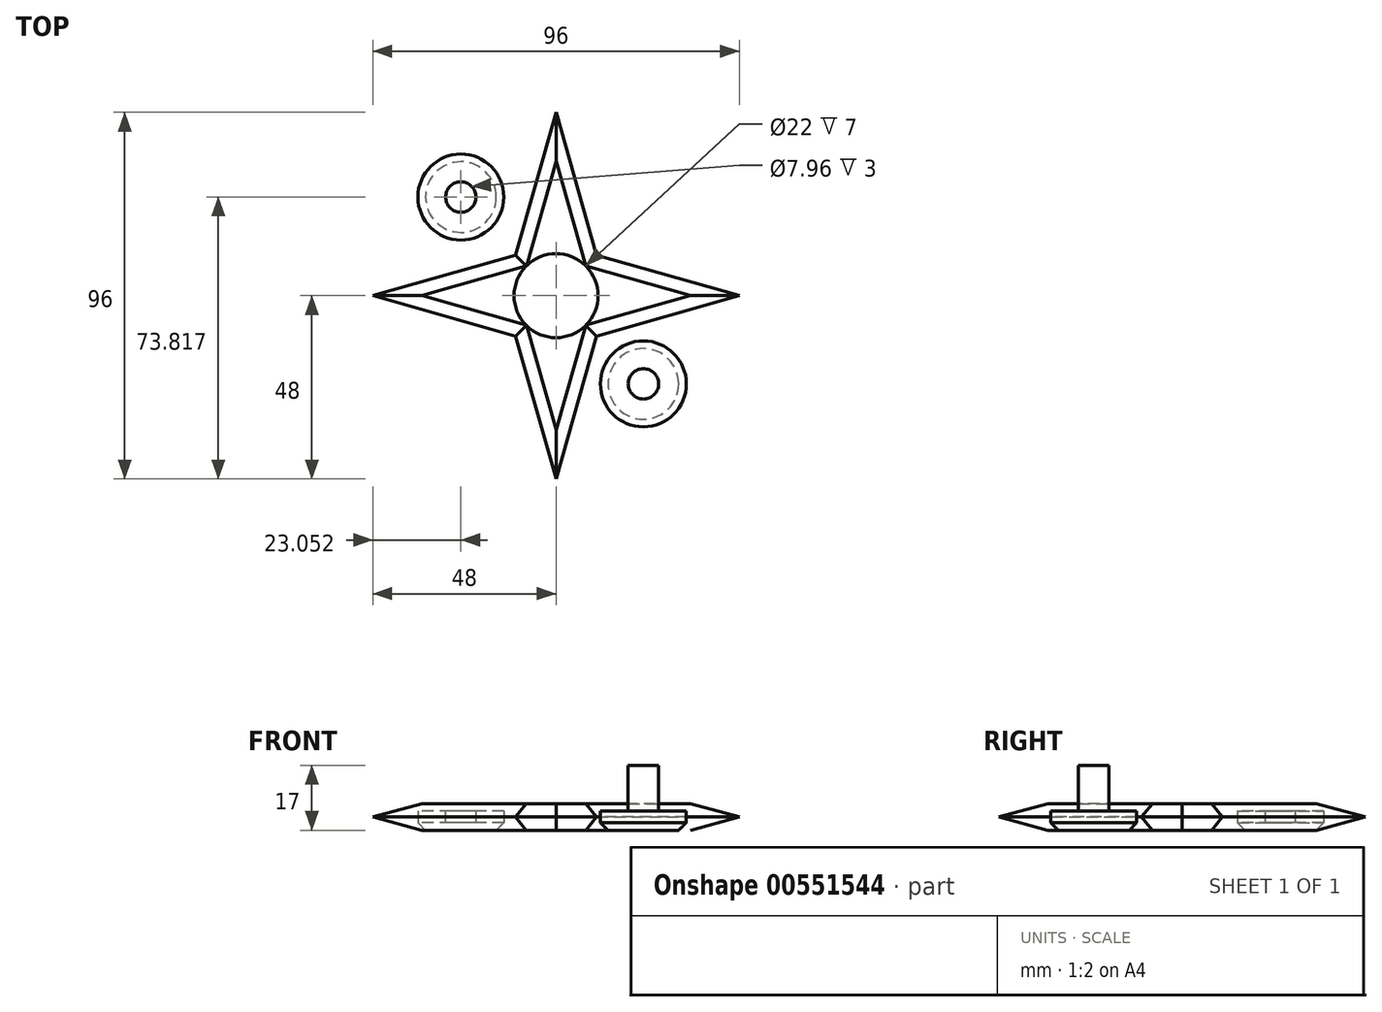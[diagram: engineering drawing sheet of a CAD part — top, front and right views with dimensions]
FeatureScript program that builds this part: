
annotation { "Feature Type Name" : "Feature", "Feature Type Description" : "" }
export const myFeature = defineFeature(function(context is Context, id is Id, definition is map)
    precondition{}
    {
        {
            var Q0;
            Q0=qCreatedBy(makeId("Top.planeOp"),FACE);
            var sketch = newSketch(context, id + "F0", { "sketchPlane" : qUnion([Q0])});
            skCircle(sketch, "E0", {"center": v(0, 0) * mm, "radius": 11 * mm});
            skLineSegment(sketch, "E1", {"start": v(-48, 0) * mm, "end": v(-10.6, 10.6) * mm});
            skLineSegment(sketch, "E2", {"start": v(-10.6, 10.6) * mm, "end": v(0, 48) * mm});
            skLineSegment(sketch, "E3", {"start": v(-48, 0) * mm, "end": v(-10.6, -10.6) * mm});
            skLineSegment(sketch, "E4", {"start": v(-10.6, -10.6) * mm, "end": v(0, -48) * mm});
            skLineSegment(sketch, "E5", {"start": v(0, -48) * mm, "end": v(10.6, -10.6) * mm});
            skLineSegment(sketch, "E6", {"start": v(10.6, -10.6) * mm, "end": v(48, 0) * mm});
            skLineSegment(sketch, "E7", {"start": v(48, 0) * mm, "end": v(10.6, 10.6) * mm});
            skLineSegment(sketch, "E8", {"start": v(10.6, 10.6) * mm, "end": v(0, 48) * mm});
            skSolve(sketch);
        }
        {
            var Q0;
            Q0=makeQuery(id+"F0.imprint","IMPRINT",FACE,{"disambiguationData":[TD([[makeQuery(id+"F0.imprint","IMPRINT",EDGE,{"derivedFrom":sQuery(id+"F0.wireOp",EDGE,"E0")}),-1.0]])]});
            extrude(context, id + "F1", {"entities" : qUnion([Q0]), "depth" : 7 * mm});
        }
        {
            var Q0;
            Q0=makeQuery(id+"F1.opExtrude","CAP_EDGE",EDGE,{"disambiguationData":[OSD([sQuery(id+"F0.wireOp",EDGE,"E2")])],"isStart":false});
            var Q1;
            Q1=makeQuery(id+"F1.opExtrude","CAP_EDGE",EDGE,{"disambiguationData":[OSD([sQuery(id+"F0.wireOp",EDGE,"E8")])],"isStart":false});
            var Q2;
            Q2=makeQuery(id+"F1.opExtrude","CAP_EDGE",EDGE,{"disambiguationData":[OSD([sQuery(id+"F0.wireOp",EDGE,"E7")])],"isStart":false});
            var Q3;
            Q3=makeQuery(id+"F1.opExtrude","CAP_EDGE",EDGE,{"disambiguationData":[OSD([sQuery(id+"F0.wireOp",EDGE,"E6")])],"isStart":false});
            var Q4;
            Q4=makeQuery(id+"F1.opExtrude","CAP_EDGE",EDGE,{"disambiguationData":[OSD([sQuery(id+"F0.wireOp",EDGE,"E5")])],"isStart":false});
            var Q5;
            Q5=makeQuery(id+"F1.opExtrude","CAP_EDGE",EDGE,{"disambiguationData":[OSD([sQuery(id+"F0.wireOp",EDGE,"E4")])],"isStart":false});
            var Q6;
            Q6=makeQuery(id+"F1.opExtrude","CAP_EDGE",EDGE,{"disambiguationData":[OSD([sQuery(id+"F0.wireOp",EDGE,"E3")])],"isStart":false});
            var Q7;
            Q7=makeQuery(id+"F1.opExtrude","CAP_EDGE",EDGE,{"disambiguationData":[OSD([sQuery(id+"F0.wireOp",EDGE,"E1")])],"isStart":false});
            var Q8;
            Q8=makeQuery(id+"F1.opExtrude","CAP_EDGE",EDGE,{"disambiguationData":[OSD([sQuery(id+"F0.wireOp",EDGE,"E3")])],"isStart":true});
            var Q9;
            Q9=makeQuery(id+"F1.opExtrude","CAP_EDGE",EDGE,{"disambiguationData":[OSD([sQuery(id+"F0.wireOp",EDGE,"E1")])],"isStart":true});
            var Q10;
            Q10=makeQuery(id+"F1.opExtrude","CAP_EDGE",EDGE,{"disambiguationData":[OSD([sQuery(id+"F0.wireOp",EDGE,"E2")])],"isStart":true});
            var Q11;
            Q11=makeQuery(id+"F1.opExtrude","CAP_EDGE",EDGE,{"disambiguationData":[OSD([sQuery(id+"F0.wireOp",EDGE,"E4")])],"isStart":true});
            var Q12;
            Q12=makeQuery(id+"F1.opExtrude","CAP_EDGE",EDGE,{"disambiguationData":[OSD([sQuery(id+"F0.wireOp",EDGE,"E5")])],"isStart":true});
            var Q13;
            Q13=makeQuery(id+"F1.opExtrude","CAP_EDGE",EDGE,{"disambiguationData":[OSD([sQuery(id+"F0.wireOp",EDGE,"E6")])],"isStart":true});
            var Q14;
            Q14=makeQuery(id+"F1.opExtrude","CAP_EDGE",EDGE,{"disambiguationData":[OSD([sQuery(id+"F0.wireOp",EDGE,"E7")])],"isStart":true});
            var Q15;
            Q15=makeQuery(id+"F1.opExtrude","CAP_EDGE",EDGE,{"disambiguationData":[OSD([sQuery(id+"F0.wireOp",EDGE,"E8")])],"isStart":true});
            chamfer(context, id + "F2", {"entities" : qUnion([Q0, Q1, Q2, Q3, Q4, Q5, Q6, Q7, Q8, Q9, Q10, Q11, Q12, Q13, Q14, Q15]), "width" : 3.5 * mm, "tangentPropagation" : true});
        }
        {
            var Q0;
            Q0=qCreatedBy(makeId("Top.planeOp"),FACE);
            var sketch = newSketch(context, id + "F3", { "sketchPlane" : qUnion([Q0])});
            skCircle(sketch, "E9", {"center": v(-50.13, 32.9) * mm, "radius": 11.25 * mm});
            skSolve(sketch);
        }
        {
            var Q0;
            Q0=makeQuery(id+"F3.imprint","IMPRINT",FACE,{"disambiguationData":[TD([[makeQuery(id+"F3.imprint","IMPRINT",EDGE,{"derivedFrom":sQuery(id+"F3.wireOp",EDGE,"E9")}),1.0]])]});
            extrude(context, id + "F4", {"entities" : qUnion([Q0]), "depth" : 5 * mm});
        }
        {
            var Q0;
            Q0=makeQuery(id+"F4.opExtrude","CAP_FACE",FACE,{"disambiguationData":[OSD([sQuery(id+"F3.wireOp",EDGE,"E9")])],"isStart":false});
            var sketch = newSketch(context, id + "F5", { "sketchPlane" : qUnion([Q0])});
            skCircle(sketch, "E10", {"center": v(-50.13, 32.9) * mm, "radius": 3.98 * mm});
            skSolve(sketch);
        }
        {
            var Q0;
            Q0=makeQuery(id+"F5.imprint","IMPRINT",FACE,{"disambiguationData":[TD([[makeQuery(id+"F5.imprint","IMPRINT",EDGE,{"derivedFrom":sQuery(id+"F5.wireOp",EDGE,"E10")}),1.0]])]});
            extrude(context, id + "F6", {"entities" : qUnion([Q0]), "operationType" : NewBodyOperationType.ADD, "depth" : 12 * mm});
        }
        {
            var Q0;
            Q0=makeQuery(id+"F4.opExtrude","CAP_EDGE",EDGE,{"disambiguationData":[OSD([sQuery(id+"F3.wireOp",EDGE,"E9")])],"isStart":true});
            chamfer(context, id + "F7", {"entities" : qUnion([Q0]), "width" : 2 * mm, "tangentPropagation" : true});
        }
        {
            var Q0;
            Q0=qCreatedBy(makeId("Top.planeOp"),FACE);
            var sketch = newSketch(context, id + "F8", { "sketchPlane" : qUnion([Q0])});
            skCircle(sketch, "E11", {"center": v(-24.95, 34.82) * mm, "radius": 11.25 * mm});
            skSolve(sketch);
        }
        {
            var Q0;
            Q0=makeQuery(id+"F8.imprint","IMPRINT",FACE,{"disambiguationData":[TD([[makeQuery(id+"F8.imprint","IMPRINT",EDGE,{"derivedFrom":sQuery(id+"F8.wireOp",EDGE,"E11")}),1.0]])]});
            extrude(context, id + "F9", {"entities" : qUnion([Q0]), "depth" : 5 * mm});
        }
        {
            var Q0;
            Q0=makeQuery(id+"F9.opExtrude","CAP_FACE",FACE,{"disambiguationData":[OSD([sQuery(id+"F8.wireOp",EDGE,"E11")])],"isStart":false});
            var sketch = newSketch(context, id + "F10", { "sketchPlane" : qUnion([Q0])});
            skCircle(sketch, "E12", {"center": v(-24.95, 34.82) * mm, "radius": 3.98 * mm});
            skSolve(sketch);
        }
        {
            var Q0;
            Q0=makeQuery(id+"F10.imprint","IMPRINT",FACE,{"disambiguationData":[TD([[makeQuery(id+"F10.imprint","IMPRINT",EDGE,{"derivedFrom":sQuery(id+"F10.wireOp",EDGE,"E12")}),1.0]])]});
            extrude(context, id + "F11", {"entities" : qUnion([Q0]), "operationType" : NewBodyOperationType.REMOVE, "oppositeDirection" : true, "depth" : 3 * mm});
        }
        {
            var Q0;
            Q0=makeQuery(id+"F9.opExtrude","CAP_EDGE",EDGE,{"disambiguationData":[OSD([sQuery(id+"F8.wireOp",EDGE,"E11")])],"isStart":true});
            chamfer(context, id + "F12", {"entities" : qUnion([Q0]), "width" : 2 * mm, "tangentPropagation" : true});
        }
        {
            var Q0;
            Q0=makeQuery(id+"F4.opExtrude","SWEPT_BODY",BODY,{"disambiguationData":[OSD([sQuery(id+"F3.wireOp",EDGE,"E9")])]});
            transform(context, id + "F13", {"entities" : qUnion([Q0]), "transformType" : TransformType.TRANSLATION_3D, "dx" : 73 * mm, "dy" : -56 * mm, "dz" : 0 * mm, "makeCopy" : false});
        }
        {
            var Q0;
            Q0=makeQuery(id+"F9.opExtrude","SWEPT_BODY",BODY,{"disambiguationData":[OSD([sQuery(id+"F8.wireOp",EDGE,"E11")])]});
            transform(context, id + "F14", {"entities" : qUnion([Q0]), "transformType" : TransformType.TRANSLATION_3D, "dx" : 0 * mm, "dy" : -9 * mm, "dz" : 0 * mm, "makeCopy" : false});
        }
    });
